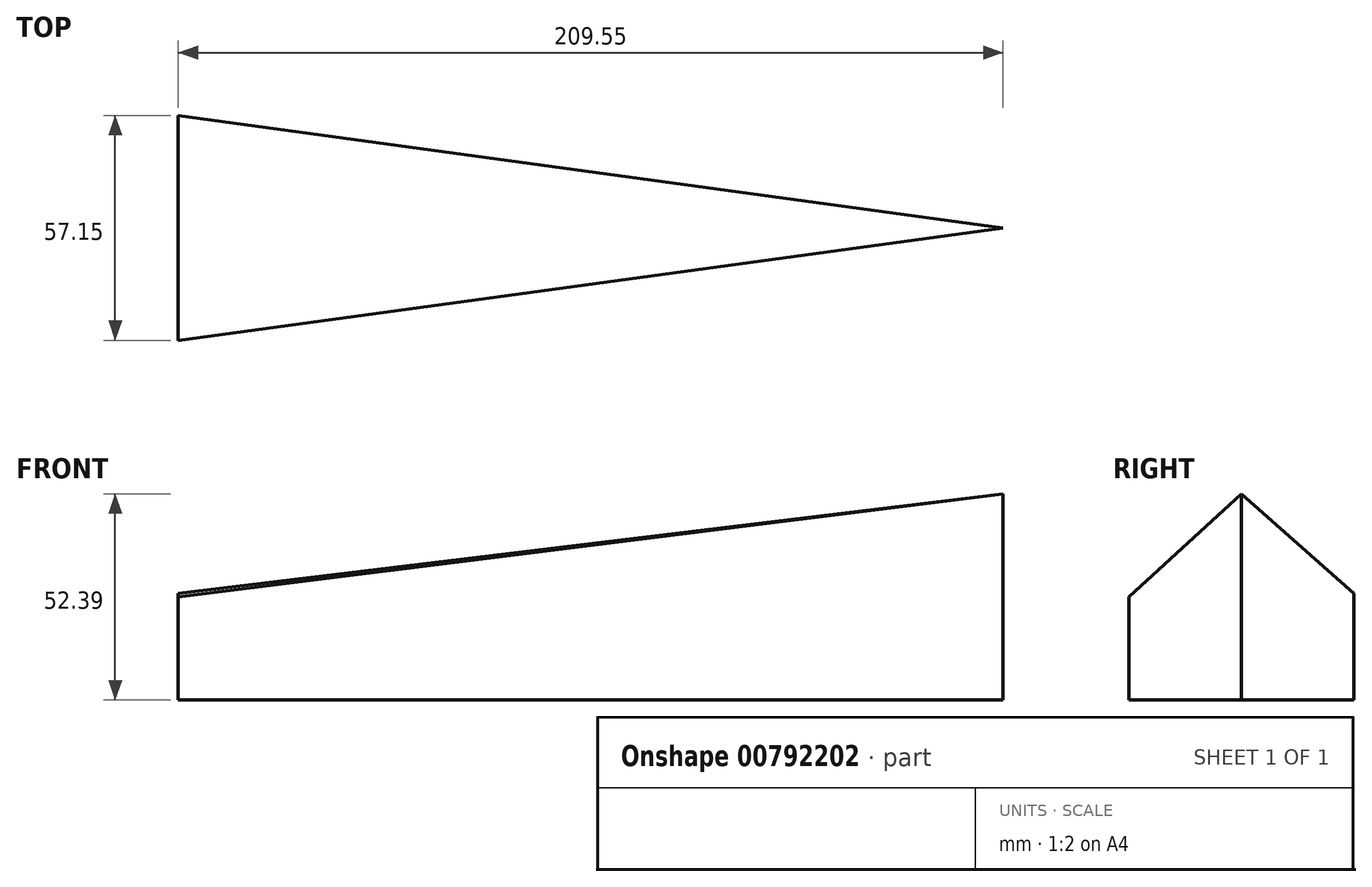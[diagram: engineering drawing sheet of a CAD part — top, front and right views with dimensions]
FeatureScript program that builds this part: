
annotation { "Feature Type Name" : "Feature", "Feature Type Description" : "" }
export const myFeature = defineFeature(function(context is Context, id is Id, definition is map)
    precondition{}
    {
        {
            var Q0;
            Q0=qCreatedBy(makeId("Front.planeOp"),FACE);
            var sketch = newSketch(context, id + "F0", { "sketchPlane" : qUnion([Q0])});
            skLineSegment(sketch, "E0", {"start": v(0, 0) * mm, "end": v(209.55, 0) * mm});
            skLineSegment(sketch, "E1", {"start": v(209.55, 0) * mm, "end": v(209.55, 52.39) * mm});
            skLineSegment(sketch, "E2", {"start": v(209.55, 52.39) * mm, "end": v(0, 52.39) * mm});
            skLineSegment(sketch, "E3", {"start": v(0, 52.39) * mm, "end": v(0, 0) * mm});
            skSolve(sketch);
        }
        {
            var Q0;
            Q0=makeQuery(id+"F0.imprint","IMPRINT",FACE,{"disambiguationData":[TD([[makeQuery(id+"F0.imprint","IMPRINT",EDGE,{"derivedFrom":sQuery(id+"F0.wireOp",EDGE,"E0")}),1.0]])]});
            extrude(context, id + "F1", {"entities" : qUnion([Q0]), "depth" : 57.15 * mm, "offsetDistance" : 25.4 * mm});
        }
        {
            var Q0;
            Q0=makeQuery(id+"F1.opExtrude","SWEPT_FACE",FACE,{"disambiguationData":[OSD([sQuery(id+"F0.wireOp",EDGE,"E2")])]});
            var sketch = newSketch(context, id + "F2", { "sketchPlane" : qUnion([Q0])});
            skLineSegment(sketch, "E4", {"start": v(209.55, -28.58) * mm, "end": v(0, -57.15) * mm});
            skLineSegment(sketch, "E5", {"start": v(0, -57.15) * mm, "end": v(209.55, -57.15) * mm});
            skLineSegment(sketch, "E6", {"start": v(209.55, -57.15) * mm, "end": v(209.55, -28.58) * mm});
            skSolve(sketch);
        }
        {
            var Q0;
            Q0=makeQuery(id+"F2.imprint","IMPRINT",FACE,{"disambiguationData":[TD([[makeQuery(id+"F2.imprint","IMPRINT",EDGE,{"derivedFrom":sQuery(id+"F2.wireOp",EDGE,"E4")}),1.0]])]});
            extrude(context, id + "F3", {"entities" : qUnion([Q0]), "operationType" : NewBodyOperationType.REMOVE, "oppositeDirection" : true, "depth" : 76.2 * mm, "offsetDistance" : 25.4 * mm});
        }
        {
            var Q0;
            Q0=makeQuery(id+"F1.opExtrude","SWEPT_FACE",FACE,{"disambiguationData":[OSD([sQuery(id+"F0.wireOp",EDGE,"E2")])]});
            var sketch = newSketch(context, id + "F4", { "sketchPlane" : qUnion([Q0])});
            skLineSegment(sketch, "E7", {"start": v(209.55, -28.58) * mm, "end": v(0, 0) * mm});
            skLineSegment(sketch, "E8", {"start": v(0, 0) * mm, "end": v(209.55, 0) * mm});
            skLineSegment(sketch, "E9", {"start": v(209.55, 0) * mm, "end": v(209.55, -28.58) * mm});
            skSolve(sketch);
        }
        {
            var Q0;
            Q0=makeQuery(id+"F4.imprint","IMPRINT",FACE,{"disambiguationData":[TD([[makeQuery(id+"F4.imprint","IMPRINT",EDGE,{"derivedFrom":sQuery(id+"F4.wireOp",EDGE,"E7")}),-1.0]])]});
            extrude(context, id + "F5", {"entities" : qUnion([Q0]), "operationType" : NewBodyOperationType.REMOVE, "oppositeDirection" : true, "depth" : 76.2 * mm, "offsetDistance" : 25.4 * mm});
        }
        {
            var Q0;
            Q0=makeQuery(id+"F3.boolean.opBoolean","COPY",FACE,{"derivedFrom":makeQuery(id+"F3.opExtrude","SWEPT_FACE",FACE,{"disambiguationData":[OSD([sQuery(id+"F2.wireOp",EDGE,"E4")])]})});
            var sketch = newSketch(context, id + "F6", { "sketchPlane" : qUnion([Q0])});
            skLineSegment(sketch, "E10", {"start": v(203.77, 52.39) * mm, "end": v(-7.72, 26.2) * mm});
            skLineSegment(sketch, "E11", {"start": v(-7.72, 26.2) * mm, "end": v(-7.72, 52.39) * mm});
            skLineSegment(sketch, "E12", {"start": v(-7.72, 52.39) * mm, "end": v(203.77, 52.39) * mm});
            skSolve(sketch);
        }
        {
            var Q0;
            Q0=makeQuery(id+"F6.imprint","IMPRINT",FACE,{"disambiguationData":[TD([[makeQuery(id+"F6.imprint","IMPRINT",EDGE,{"derivedFrom":sQuery(id+"F6.wireOp",EDGE,"E10")}),-1.0]])]});
            extrude(context, id + "F7", {"entities" : qUnion([Q0]), "operationType" : NewBodyOperationType.REMOVE, "oppositeDirection" : true, "depth" : 72.64 * mm, "offsetDistance" : 25.4 * mm});
        }
        {
            var Q0;
            Q0=makeQuery(id+"F3.boolean.opBoolean","COPY",FACE,{"derivedFrom":makeQuery(id+"F3.opExtrude","SWEPT_FACE",FACE,{"disambiguationData":[OSD([sQuery(id+"F2.wireOp",EDGE,"E4")])]})});
            var sketch = newSketch(context, id + "F8", { "sketchPlane" : qUnion([Q0])});
            skLineSegment(sketch, "E13", {"start": v(-7.72, 26.2) * mm, "end": v(203.77, 52.39) * mm});
            skLineSegment(sketch, "E14", {"start": v(203.77, 52.39) * mm, "end": v(203.77, 0) * mm});
            skLineSegment(sketch, "E15", {"start": v(203.77, 0) * mm, "end": v(-25.23, 0) * mm});
            skLineSegment(sketch, "E16", {"start": v(-25.23, 0) * mm, "end": v(-7.72, 26.2) * mm});
            skSolve(sketch);
        }
        {
            var Q0;
            Q0=makeQuery(id+"F8.imprint","IMPRINT",FACE,{"disambiguationData":[TD([[makeQuery(id+"F8.imprint","IMPRINT",EDGE,{"derivedFrom":sQuery(id+"F8.wireOp",EDGE,"E13")}),1.0]])]});
            var Q1;
            {var subQ3=sQuery(id+"F8.wireOp",EDGE,"E16");Q1=makeQuery(id+"F8.imprint","IMPRINT",FACE,{"disambiguationData":[TD([[makeQuery(id+"F8.imprint","IMPRINT",EDGE,{"derivedFrom":subQ3}),-1.0]])]});}
            extrude(context, id + "F9", {"entities" : qUnion([Q0, Q1]), "operationType" : NewBodyOperationType.REMOVE, "depth" : 19.3 * mm, "offsetDistance" : 25.4 * mm});
        }
    });
